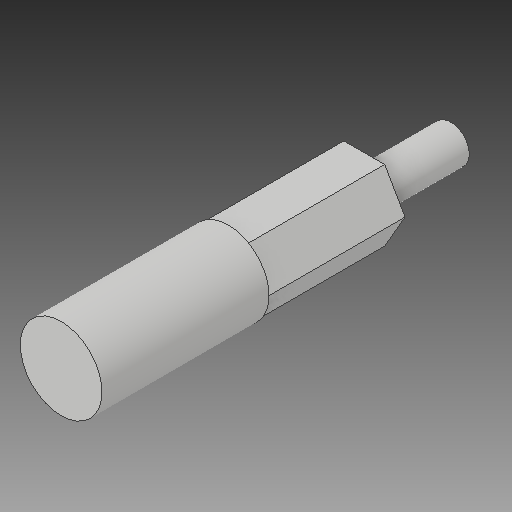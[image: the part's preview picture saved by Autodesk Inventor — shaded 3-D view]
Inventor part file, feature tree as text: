
AUTODESK INVENTOR PART (.ipt)
format: ipt  version: 2019 (Build 230136000, 136)  size: 103,936 bytes
history: native  units: in
note: dims shown in document units (in); Inventor stores cm internally (conversion verified against a paired STEP export)
features: other x3, sketch x3, plane x1
ambient origin geometry x8: Origin, YZ Plane, XZ Plane, XY Plane, X Axis, Y Axis, Z Axis, Center Point
bodies: Solid1 (feature_tree)
feature tree (7):
  other  "Wheel_Pin.ipt"
  other  "Solid1::Wheel_Pin.ipt"
  other  "TaggingFeature1"
  sketch  "Sketch1"  dims[d0=0.3937in]
  sketch  "Sketch2"
  sketch  "Sketch3"
  plane  "Work Plane1"
